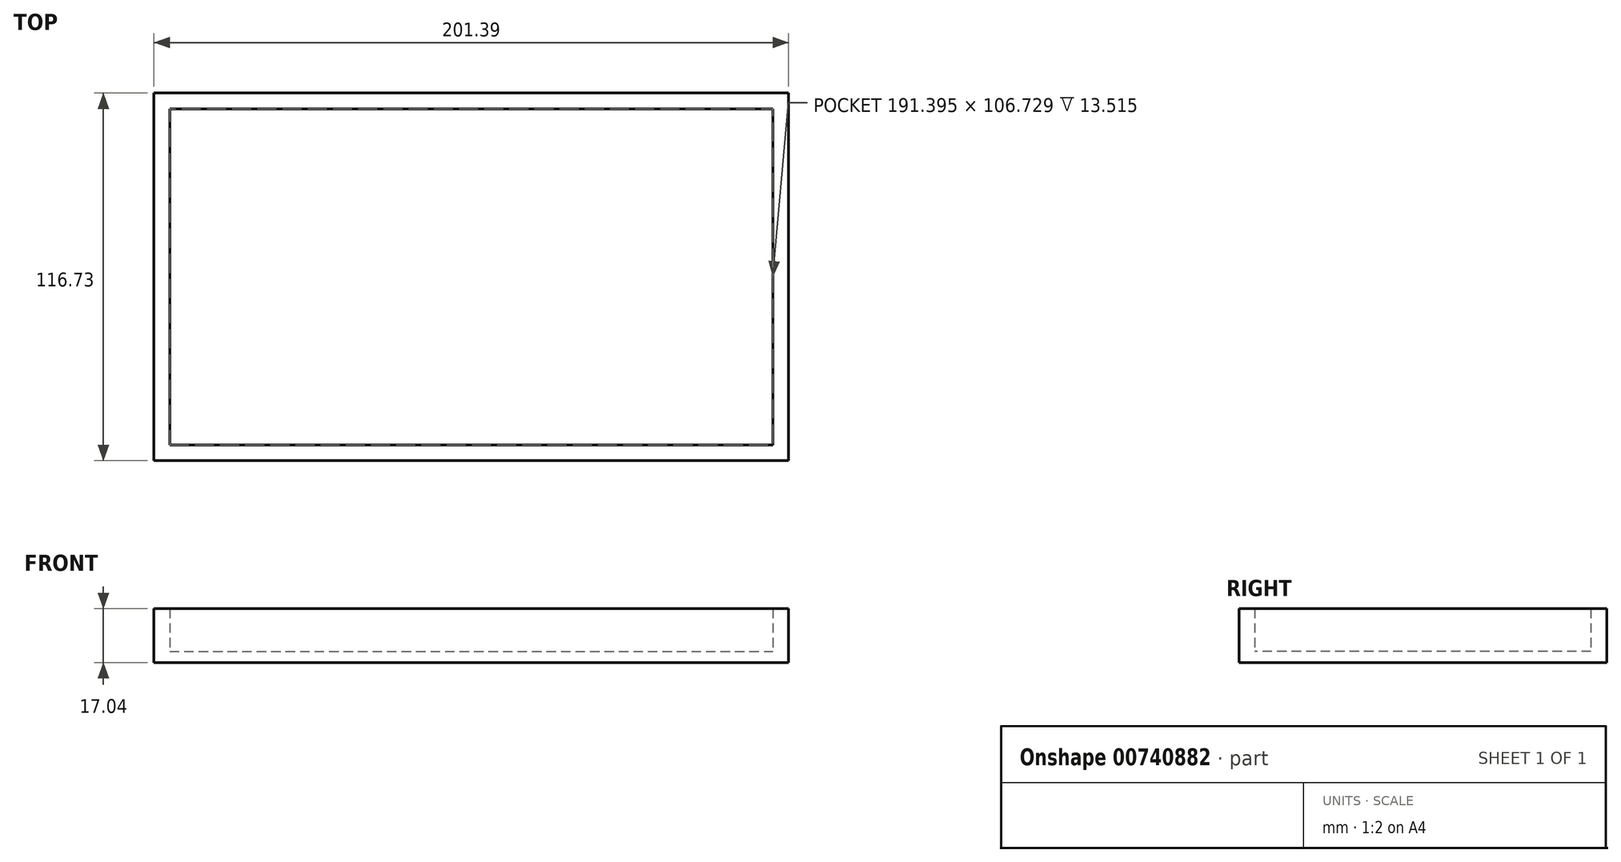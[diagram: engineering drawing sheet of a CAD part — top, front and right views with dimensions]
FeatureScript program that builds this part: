
annotation { "Feature Type Name" : "Feature", "Feature Type Description" : "" }
export const myFeature = defineFeature(function(context is Context, id is Id, definition is map)
    precondition{}
    {
        {
            var Q0;
            Q0=qCreatedBy(makeId("Top.planeOp"),FACE);
            var sketch = newSketch(context, id + "F0", { "sketchPlane" : qUnion([Q0])});
            skLineSegment(sketch, "E0.bottom", {"start": v(-5, 5) * mm, "end": v(196.4, 5) * mm});
            skLineSegment(sketch, "E0.top", {"start": v(-5, -111.73) * mm, "end": v(196.4, -111.73) * mm});
            skLineSegment(sketch, "E0.left", {"start": v(-5, 5) * mm, "end": v(-5, -111.73) * mm});
            skLineSegment(sketch, "E0.right", {"start": v(196.4, 5) * mm, "end": v(196.4, -111.73) * mm});
            skSolve(sketch);
        }
        {
            var Q0;
            Q0=makeQuery(id+"F0.imprint","IMPRINT",FACE,{"disambiguationData":[TD([[makeQuery(id+"F0.imprint","IMPRINT",EDGE,{"derivedFrom":sQuery(id+"F0.wireOp",EDGE,"E0.bottom")}),-1.0]])]});
            extrude(context, id + "F1", {"entities" : qUnion([Q0]), "endBound" : BoundingType.SYMMETRIC, "oppositeDirection" : true, "depth" : 17.03 * mm, "offsetDistance" : 25 * mm});
        }
        {
            var Q0;
            Q0=qCreatedBy(makeId("Top.planeOp"),FACE);
            var sketch = newSketch(context, id + "F2", { "sketchPlane" : qUnion([Q0])});
            skLineSegment(sketch, "E1.bottom", {"start": v(0, 0) * mm, "end": v(191.4, 0) * mm});
            skLineSegment(sketch, "E1.top", {"start": v(0, -106.73) * mm, "end": v(191.4, -106.73) * mm});
            skLineSegment(sketch, "E1.left", {"start": v(0, 0) * mm, "end": v(0, -106.73) * mm});
            skLineSegment(sketch, "E1.right", {"start": v(191.4, 0) * mm, "end": v(191.4, -106.73) * mm});
            skSolve(sketch);
        }
        {
            var Q0;
            Q0=makeQuery(id+"F2.imprint","IMPRINT",FACE,{"disambiguationData":[TD([[makeQuery(id+"F2.imprint","IMPRINT",EDGE,{"derivedFrom":sQuery(id+"F2.wireOp",EDGE,"E1.bottom")}),-1.0]])]});
            var Q1;
            Q1=makeQuery(id+"F1.opExtrude","CAP_FACE",FACE,{"disambiguationData":[OSD([sQuery(id+"F0.wireOp",EDGE,"E0.bottom"),sQuery(id+"F0.wireOp",EDGE,"E0.top"),sQuery(id+"F0.wireOp",EDGE,"E0.left"),sQuery(id+"F0.wireOp",EDGE,"E0.right")])],"isStart":true});
            extrude(context, id + "F3", {"entities" : qUnion([Q0]), "operationType" : NewBodyOperationType.REMOVE, "endBound" : BoundingType.UP_TO_SURFACE, "depth" : 17 * mm, "endBoundEntityFace" : qUnion([Q1]), "offsetDistance" : 12 * mm, "hasSecondDirection" : true, "secondDirectionOppositeDirection" : true, "secondDirectionDepth" : 5 * mm});
        }
    });
